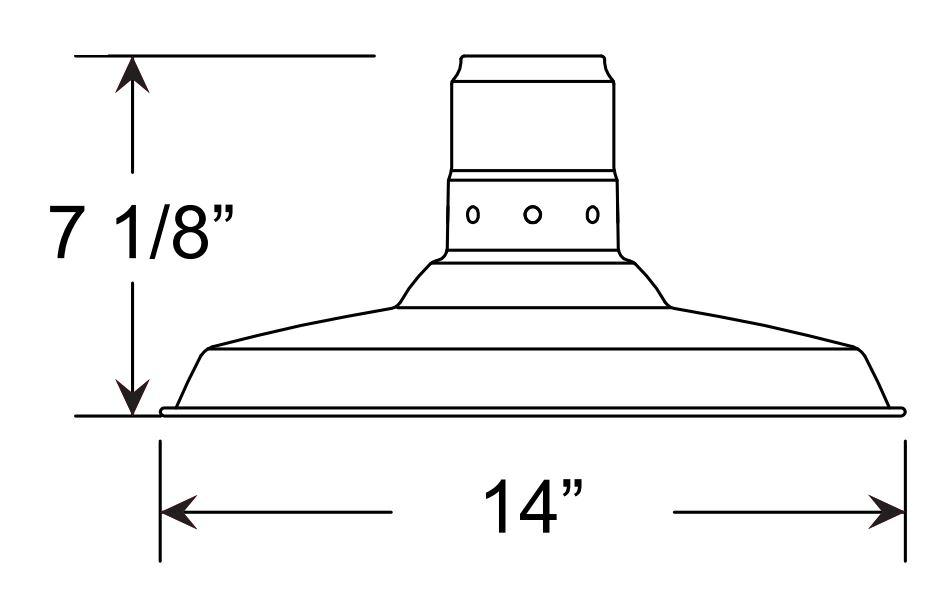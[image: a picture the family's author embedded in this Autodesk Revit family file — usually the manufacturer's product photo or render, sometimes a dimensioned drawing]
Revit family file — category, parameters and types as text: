
# Revit family: OSGG(24,30,36) LED
name_source: partatom
category: Lighting Fixtures
units: mm (PartAtom-declared; Revit-internal decimal feet)

## family parameters
Always vertical = Yes
Cut with Voids When Loaded = No
Light Source = Yes
OmniClass Number = 23.80.70.00
OmniClass Title = Lighting
Part Type = Normal
Room Calculation Point = No
Round Connector Dimension = Use Diameter
Shared = No
Work Plane-Based = No

## types (3) — shared parameters
Body Colour = Spun aluminium
Body Material = body
Bulb = Bulb
CRI = >90
Color Filter = 16777215
Construction Material = Heavy Duty spun aluminum.
Default Elevation = 0' - 0"
Description = 120-277 Voltage
Dimming = 1%
Dimming Lamp Color Temperature Shift = <None>
Efficiency = 65-125 lumens per watt
Inside body material = INSIDE BODY
Lamp = LED
Life = L70 50,000 hours
Load Classification = Lighting
Manufacturer = ANP Lighting
Photometric Web File = OSGG36M037LDDW35K.ies
Power Factor = 1
Tilt Angle = 90.00°
URL = https://www.anplighting.com
Voltage = 277 V
Warranty = 5 year limited warranty

## per-type parameters (varying)
| type | Apparent Load | Fixture Diameter | Fixture Height | OSGG24 | OSGG30 | OSGG36 | Wattage Comments | Weight |
| OSGG 24 | 24 VA | 2' - 0" | 2' - 2" | Yes | No | No | 24W | 21.5 lbs |
| OSGG 30 | 24 VA | 2' - 6" | 3' - 0" | No | Yes | No | 24W | 33 lbs |
| OSGG 36 | 37 VA | 3' - 0" | 3' - 4" | No | No | Yes | 37W | 43.5 lbs |

note: column(s) folded — value = type name in every type: Model

## geometry (parser evidence)
native form markers: Sweep x45
no freeform markers — native parametric forms only
